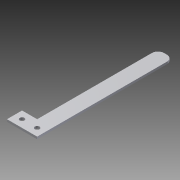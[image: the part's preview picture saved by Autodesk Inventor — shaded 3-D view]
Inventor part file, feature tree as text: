
AUTODESK INVENTOR PART (.ipt)
format: ipt  version: 2015 (Build 190159000, 159)  size: 123,904 bytes
history: native  units: mm
features: sketch x3, extrude x2, other x1, fillet x1, hole x1
ambient origin geometry x8: Origin, YZ Plane, XZ Plane, XY Plane, X Axis, Y Axis, Z Axis, Center Point
bodies: Body1 (feature_tree)
feature tree (8):
  other  "ソリッド1"
  extrude  "押し出し1"  Depth=10.0mm
  fillet  "フィレット1"  Radius=80.0mm
  extrude  "押し出し2"  Depth=1.5mm TaperAngle=0.0deg
  hole  "穴2"  [1 undecoded]
  sketch  "スケッチ1"
  sketch  "スケッチ2"
  sketch  "スケッチ9"
note: 1 required parameter value undecoded (feature->parameter linkage not recoverable at this tier; creation-order binding heuristic only, values carry confidence <= 0.55)
